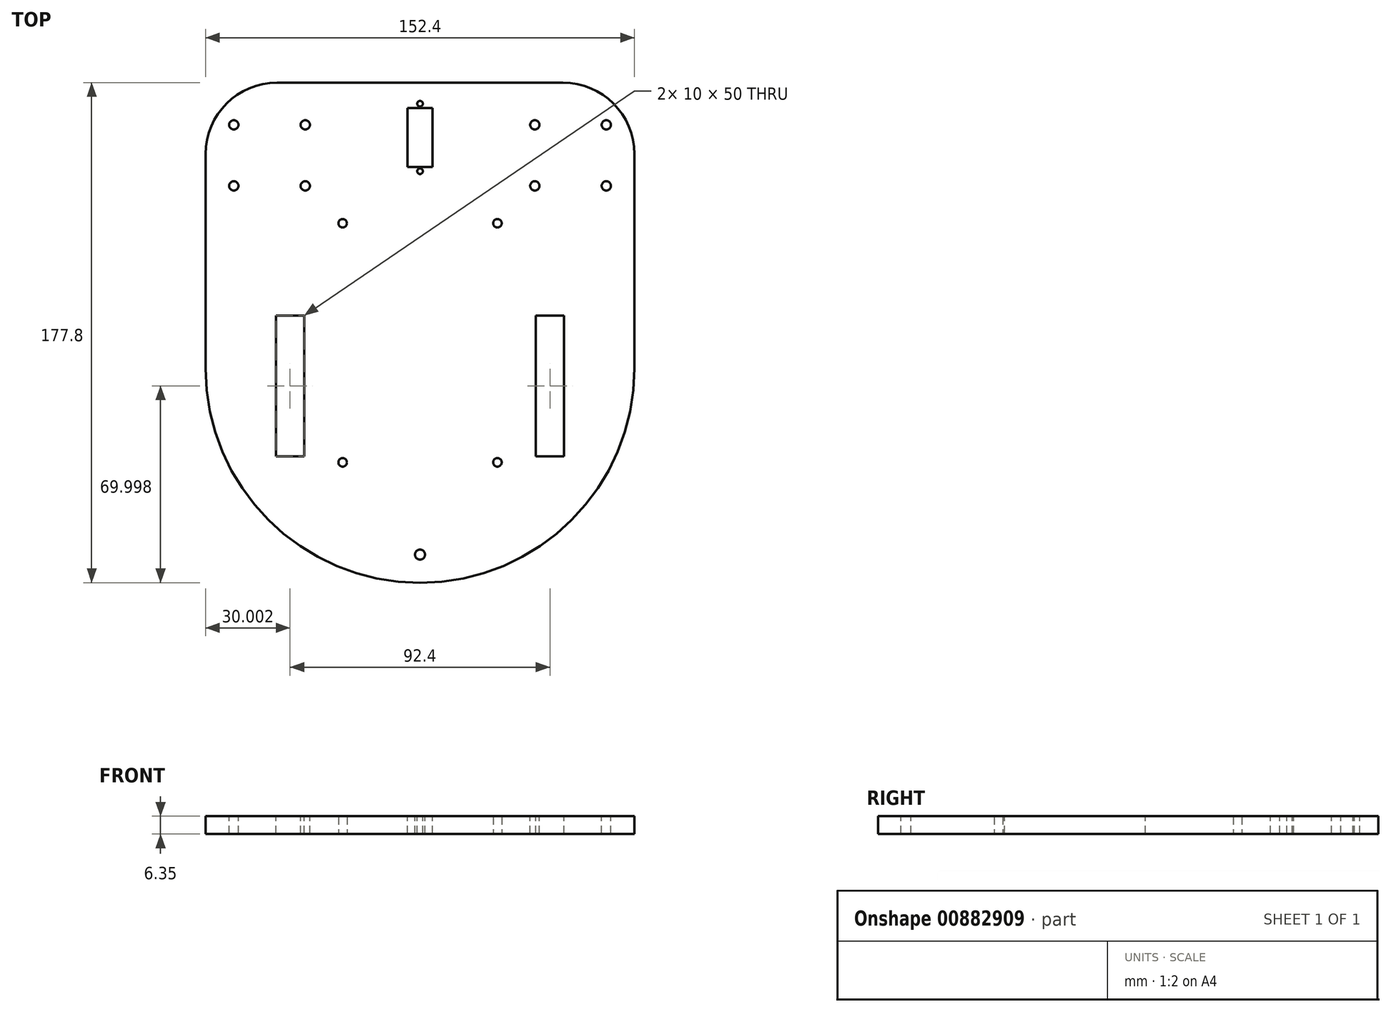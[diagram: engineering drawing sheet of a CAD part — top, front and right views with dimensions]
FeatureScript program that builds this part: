
annotation { "Feature Type Name" : "Feature", "Feature Type Description" : "" }
export const myFeature = defineFeature(function(context is Context, id is Id, definition is map)
    precondition{}
    {
        {
            var Q0;
            Q0=qCreatedBy(makeId("Top.planeOp"),FACE);
            var sketch = newSketch(context, id + "F0", { "sketchPlane" : qUnion([Q0])});
            skLineSegment(sketch, "E0.bottom", {"start": v(-65.4, 81.7) * mm, "end": v(36.2, 81.7) * mm});
            skLineSegment(sketch, "E0.top", {"start": v(-14.6, -96.1) * mm, "end": v(-14.6, -96.1) * mm});
            skLineSegment(sketch, "E0.left", {"start": v(-90.8, 56.3) * mm, "end": v(-90.8, -19.9) * mm});
            skLineSegment(sketch, "E0.right", {"start": v(61.6, 56.3) * mm, "end": v(61.6, -19.9) * mm});
            skPoint(sketch, "E1.visualSharp", {"position": v(-90.8, 81.7) * mm});
            skArc(sketch, "E1.filletArc", {"start": v(-65.4, 81.7) * mm, "mid": v(-83.37, 74.27) * mm, "end": v(-90.8, 56.3) * mm});
            skPoint(sketch, "E2.visualSharp", {"position": v(61.6, 81.7) * mm});
            skArc(sketch, "E2.filletArc", {"start": v(61.6, 56.3) * mm, "mid": v(54.15, 74.27) * mm, "end": v(36.2, 81.7) * mm});
            skPoint(sketch, "E3.visualSharp", {"position": v(-90.8, -96.1) * mm});
            skArc(sketch, "E3.filletArc", {"start": v(-90.8, -19.9) * mm, "mid": v(-68.49, -73.77) * mm, "end": v(-14.6, -96.1) * mm});
            skPoint(sketch, "E4.visualSharp", {"position": v(61.6, -96.1) * mm});
            skArc(sketch, "E4.filletArc", {"start": v(-14.6, -96.1) * mm, "mid": v(39.27, -73.77) * mm, "end": v(61.6, -19.9) * mm});
            skCircle(sketch, "E5", {"center": v(-42.1, 31.7) * mm, "radius": 1.52 * mm});
            skLineSegment(sketch, "E6", {"start": v(-14.6, 81.7) * mm, "end": v(-14.6, -96.1) * mm, "construction": true});
            skCircle(sketch, "E7.0.1.0", {"center": v(-42.1, -53.3) * mm, "radius": 1.52 * mm});
            skCircle(sketch, "E7.1.0.0", {"center": v(12.9, 31.7) * mm, "radius": 1.52 * mm});
            skCircle(sketch, "E7.1.1.0", {"center": v(12.9, -53.3) * mm, "radius": 1.52 * mm});
            skCircle(sketch, "E7.2.0.0", {"center": v(67.9, 31.7) * mm, "radius": 1.52 * mm});
            skCircle(sketch, "E7.2.1.0", {"center": v(67.9, -53.3) * mm, "radius": 1.52 * mm});
            skLineSegment(sketch, "E7.direction1", {"start": v(-42.1, 31.7) * mm, "end": v(12.9, 31.7) * mm, "construction": true});
            skLineSegment(sketch, "E7.direction2", {"start": v(-42.1, 31.7) * mm, "end": v(-42.1, -53.3) * mm, "construction": true});
            skSolve(sketch);
        }
        {
            var Q0;
            Q0=makeQuery(id+"F0.imprint","IMPRINT",FACE,{"disambiguationData":[TD([[makeQuery(id+"F0.imprint","IMPRINT",EDGE,{"derivedFrom":sQuery(id+"F0.wireOp",EDGE,"E0.bottom")}),-1.0]])]});
            extrude(context, id + "F1", {"entities" : qUnion([Q0]), "depth" : 6.35 * mm, "offsetDistance" : 25 * mm});
        }
        {
            var Q0;
            Q0=makeQuery(id+"F1.opExtrude","CAP_FACE",FACE,{"disambiguationData":[OSD([sQuery(id+"F0.wireOp",EDGE,"E0.bottom"),sQuery(id+"F0.wireOp",EDGE,"E0.left"),sQuery(id+"F0.wireOp",EDGE,"E0.right"),sQuery(id+"F0.wireOp",EDGE,"E1.filletArc"),sQuery(id+"F0.wireOp",EDGE,"E2.filletArc"),sQuery(id+"F0.wireOp",EDGE,"E3.filletArc"),sQuery(id+"F0.wireOp",EDGE,"E4.filletArc"),sQuery(id+"F0.wireOp",EDGE,"E5"),sQuery(id+"F0.wireOp",EDGE,"E7.0.1.0"),sQuery(id+"F0.wireOp",EDGE,"E7.1.0.0"),sQuery(id+"F0.wireOp",EDGE,"E7.1.1.0")])],"isStart":false});
            var sketch = newSketch(context, id + "F2", { "sketchPlane" : qUnion([Q0])});
            skCircle(sketch, "E8", {"center": v(-80.8, 66.7) * mm, "radius": 1.65 * mm});
            skCircle(sketch, "E9.0.1.0", {"center": v(-80.8, 45) * mm, "radius": 1.65 * mm});
            skCircle(sketch, "E9.1.0.0", {"center": v(-55.4, 66.7) * mm, "radius": 1.65 * mm});
            skCircle(sketch, "E9.1.1.0", {"center": v(-55.4, 45) * mm, "radius": 1.65 * mm});
            skLineSegment(sketch, "E9.direction1", {"start": v(-80.8, 66.7) * mm, "end": v(-55.4, 66.7) * mm, "construction": true});
            skLineSegment(sketch, "E9.direction2", {"start": v(-80.8, 66.7) * mm, "end": v(-80.8, 45) * mm, "construction": true});
            skLineSegment(sketch, "E10", {"start": v(-14.6, 81.7) * mm, "end": v(-14.6, 18.5) * mm, "construction": true});
            skCircle(sketch, "E11.MirrorC", {"center": v(26.2, 66.7) * mm, "radius": 1.65 * mm});
            skCircle(sketch, "E12.MirrorC", {"center": v(51.6, 66.7) * mm, "radius": 1.65 * mm});
            skCircle(sketch, "E13.MirrorC", {"center": v(26.2, 45) * mm, "radius": 1.65 * mm});
            skCircle(sketch, "E14.MirrorC", {"center": v(51.6, 45) * mm, "radius": 1.65 * mm});
            skSolve(sketch);
        }
        {
            var Q0;
            Q0 = qSketchRegion(id + "F2", true);
            extrude(context, id + "F3", {"entities" : qUnion([Q0]), "operationType" : NewBodyOperationType.REMOVE, "endBound" : BoundingType.THROUGH_ALL, "oppositeDirection" : true, "depth" : 25 * mm, "offsetDistance" : 25 * mm});
        }
        {
            var Q0;
            Q0=makeQuery(id+"F1.opExtrude","CAP_FACE",FACE,{"disambiguationData":[OSD([sQuery(id+"F0.wireOp",EDGE,"E0.bottom"),sQuery(id+"F0.wireOp",EDGE,"E0.left"),sQuery(id+"F0.wireOp",EDGE,"E0.right"),sQuery(id+"F0.wireOp",EDGE,"E1.filletArc"),sQuery(id+"F0.wireOp",EDGE,"E2.filletArc"),sQuery(id+"F0.wireOp",EDGE,"E3.filletArc"),sQuery(id+"F0.wireOp",EDGE,"E4.filletArc"),sQuery(id+"F0.wireOp",EDGE,"E5"),sQuery(id+"F0.wireOp",EDGE,"E7.0.1.0"),sQuery(id+"F0.wireOp",EDGE,"E7.1.0.0"),sQuery(id+"F0.wireOp",EDGE,"E7.1.1.0")])],"isStart":false});
            var sketch = newSketch(context, id + "F4", { "sketchPlane" : qUnion([Q0])});
            skCircle(sketch, "E15", {"center": v(-14.6, -86.1) * mm, "radius": 1.78 * mm});
            skSolve(sketch);
        }
        {
            var Q0;
            Q0=makeQuery(id+"F4.imprint","IMPRINT",FACE,{"disambiguationData":[TD([[makeQuery(id+"F4.imprint","IMPRINT",EDGE,{"derivedFrom":sQuery(id+"F4.wireOp",EDGE,"E15")}),1.0]])]});
            extrude(context, id + "F5", {"entities" : qUnion([Q0]), "operationType" : NewBodyOperationType.REMOVE, "endBound" : BoundingType.THROUGH_ALL, "oppositeDirection" : true, "depth" : 25 * mm, "offsetDistance" : 25 * mm});
        }
        {
            var Q0;
            Q0=makeQuery(id+"F1.opExtrude","CAP_FACE",FACE,{"disambiguationData":[OSD([sQuery(id+"F0.wireOp",EDGE,"E0.bottom"),sQuery(id+"F0.wireOp",EDGE,"E0.left"),sQuery(id+"F0.wireOp",EDGE,"E0.right"),sQuery(id+"F0.wireOp",EDGE,"E1.filletArc"),sQuery(id+"F0.wireOp",EDGE,"E2.filletArc"),sQuery(id+"F0.wireOp",EDGE,"E3.filletArc"),sQuery(id+"F0.wireOp",EDGE,"E4.filletArc"),sQuery(id+"F0.wireOp",EDGE,"E5"),sQuery(id+"F0.wireOp",EDGE,"E7.0.1.0"),sQuery(id+"F0.wireOp",EDGE,"E7.1.0.0"),sQuery(id+"F0.wireOp",EDGE,"E7.1.1.0")])],"isStart":false});
            var sketch = newSketch(context, id + "F6", { "sketchPlane" : qUnion([Q0])});
            skLineSegment(sketch, "E16.bottom", {"start": v(-65.8, -1.1) * mm, "end": v(-55.8, -1.1) * mm});
            skLineSegment(sketch, "E16.top", {"start": v(-65.8, -51.1) * mm, "end": v(-55.8, -51.1) * mm});
            skLineSegment(sketch, "E16.left", {"start": v(-65.8, -1.1) * mm, "end": v(-65.8, -51.1) * mm});
            skLineSegment(sketch, "E16.right", {"start": v(-55.8, -1.1) * mm, "end": v(-55.8, -51.1) * mm});
            skLineSegment(sketch, "E17", {"start": v(-14.6, 81.7) * mm, "end": v(-14.6, -96.1) * mm, "construction": true});
            skLineSegment(sketch, "E18.MirrorCS", {"start": v(26.6, -1.1) * mm, "end": v(26.6, -51.1) * mm});
            skLineSegment(sketch, "E19.MirrorCS", {"start": v(36.6, -1.1) * mm, "end": v(26.6, -1.1) * mm});
            skLineSegment(sketch, "E20.MirrorCS", {"start": v(36.6, -1.1) * mm, "end": v(36.6, -51.1) * mm});
            skLineSegment(sketch, "E21.MirrorCS", {"start": v(36.6, -51.1) * mm, "end": v(26.6, -51.1) * mm});
            skLineSegment(sketch, "E22.bottom", {"start": v(-19.1, 72.7) * mm, "end": v(-10.1, 72.7) * mm});
            skLineSegment(sketch, "E22.top", {"start": v(-19.1, 51.7) * mm, "end": v(-10.1, 51.7) * mm});
            skLineSegment(sketch, "E22.left", {"start": v(-19.1, 72.7) * mm, "end": v(-19.1, 51.7) * mm});
            skLineSegment(sketch, "E22.right", {"start": v(-10.1, 72.7) * mm, "end": v(-10.1, 51.7) * mm});
            skCircle(sketch, "E23", {"center": v(-14.6, 74.2) * mm, "radius": 1 * mm});
            skCircle(sketch, "E24", {"center": v(-14.6, 50.2) * mm, "radius": 1 * mm});
            skSolve(sketch);
        }
        {
            var Q0;
            Q0=makeQuery(id+"F6.imprint","IMPRINT",FACE,{"disambiguationData":[TD([[makeQuery(id+"F6.imprint","IMPRINT",EDGE,{"derivedFrom":sQuery(id+"F6.wireOp",EDGE,"E16.bottom")}),-1.0]])]});
            var Q1;
            Q1=makeQuery(id+"F6.imprint","IMPRINT",FACE,{"disambiguationData":[TD([[makeQuery(id+"F6.imprint","IMPRINT",EDGE,{"derivedFrom":sQuery(id+"F6.wireOp",EDGE,"E18.MirrorCS")}),1.0]])]});
            var Q2;
            Q2=makeQuery(id+"F6.imprint","IMPRINT",FACE,{"disambiguationData":[TD([[makeQuery(id+"F6.imprint","IMPRINT",EDGE,{"derivedFrom":sQuery(id+"F6.wireOp",EDGE,"E22.bottom")}),-1.0]])]});
            var Q3;
            Q3=makeQuery(id+"F6.imprint","IMPRINT",FACE,{"disambiguationData":[TD([[makeQuery(id+"F6.imprint","IMPRINT",EDGE,{"derivedFrom":sQuery(id+"F6.wireOp",EDGE,"E23")}),1.0]])]});
            var Q4;
            Q4=makeQuery(id+"F6.imprint","IMPRINT",FACE,{"disambiguationData":[TD([[makeQuery(id+"F6.imprint","IMPRINT",EDGE,{"derivedFrom":sQuery(id+"F6.wireOp",EDGE,"E24")}),1.0]])]});
            extrude(context, id + "F7", {"entities" : qUnion([Q0, Q1, Q2, Q3, Q4]), "operationType" : NewBodyOperationType.REMOVE, "endBound" : BoundingType.THROUGH_ALL, "oppositeDirection" : true, "depth" : 25 * mm, "offsetDistance" : 25 * mm});
        }
    });
